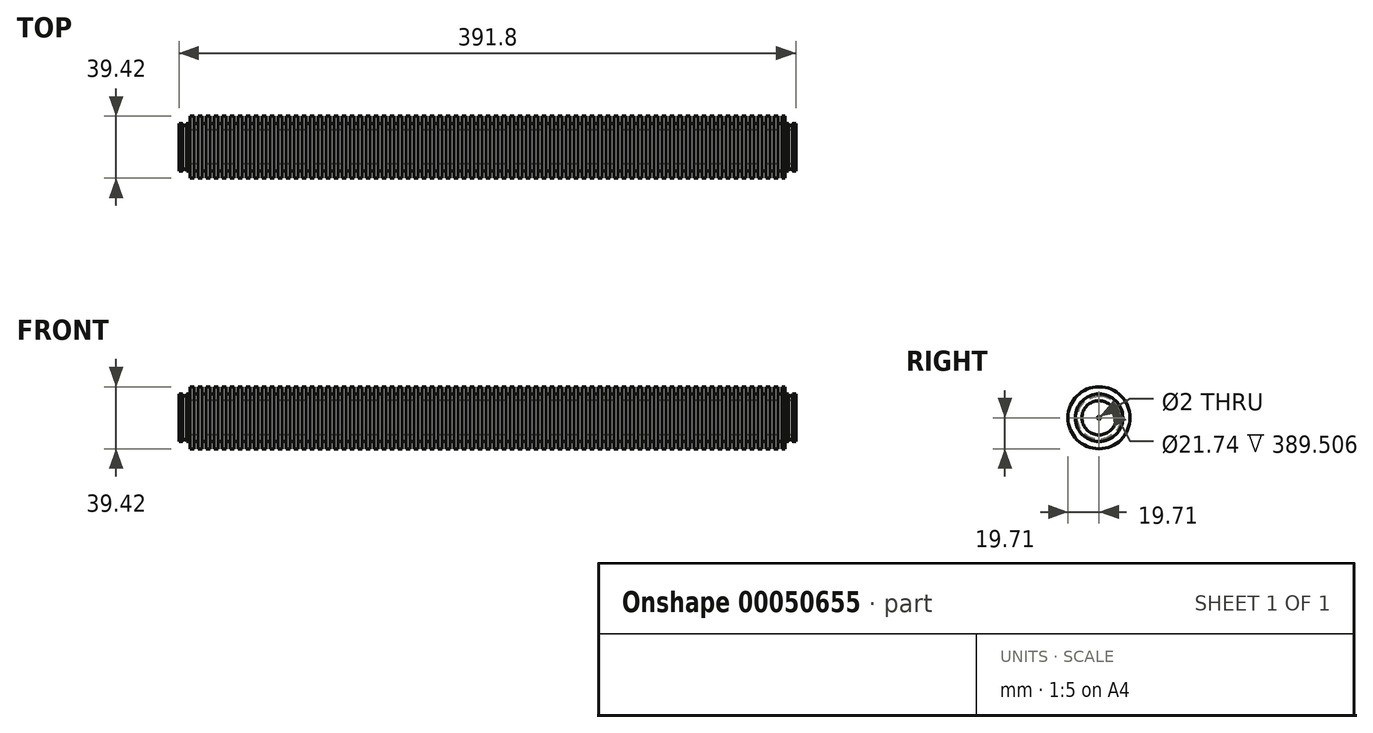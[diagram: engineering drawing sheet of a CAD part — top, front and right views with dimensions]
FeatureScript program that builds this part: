
annotation { "Feature Type Name" : "Feature", "Feature Type Description" : "" }
export const myFeature = defineFeature(function(context is Context, id is Id, definition is map)
    precondition{}
    {
        {
            var Q0;
            Q0=qCreatedBy(makeId("Front.planeOp"),FACE);
            var sketch = newSketch(context, id + "F0", { "sketchPlane" : qUnion([Q0])});
            skLineSegment(sketch, "E0", {"start": v(0, 15.1) * mm, "end": v(2.23, 15.1) * mm});
            skLineSegment(sketch, "E1", {"start": v(7, 15.1) * mm, "end": v(7, 19.7) * mm});
            skLineSegment(sketch, "E2", {"start": v(7, 19.7) * mm, "end": v(9.54, 19.7) * mm});
            skLineSegment(sketch, "E3", {"start": v(384.8, 19.71) * mm, "end": v(384.8, 15.1) * mm});
            skLineSegment(sketch, "E4", {"start": v(391.8, 15.1) * mm, "end": v(391.8, 10.87) * mm});
            skLineSegment(sketch, "E5", {"start": v(391.8, 10.87) * mm, "end": v(2.29, 10.87) * mm});
            skLineSegment(sketch, "E6", {"start": v(0, 15.1) * mm, "end": v(0, 10.87) * mm});
            skArc(sketch, "E7", {"start": v(2.23, 15.1) * mm, "mid": v(3.5, 13.83) * mm, "end": v(4.77, 15.1) * mm});
            skLineSegment(sketch, "E8.trimOffspring", {"start": v(4.77, 15.1) * mm, "end": v(7, 15.1) * mm});
            skLineSegment(sketch, "E9", {"start": v(384.8, 15.1) * mm, "end": v(387.03, 15.1) * mm});
            skArc(sketch, "E10", {"start": v(387.03, 15.1) * mm, "mid": v(388.3, 13.83) * mm, "end": v(389.57, 15.1) * mm});
            skLineSegment(sketch, "E11.trimOffspring", {"start": v(389.57, 15.1) * mm, "end": v(391.8, 15.1) * mm});
            skLineSegment(sketch, "E12", {"start": v(0, 10.87) * mm, "end": v(0, 1) * mm});
            skLineSegment(sketch, "E13", {"start": v(0, 1) * mm, "end": v(2.29, 1) * mm});
            skLineSegment(sketch, "E14", {"start": v(2.29, 1) * mm, "end": v(2.29, 10.87) * mm});
            skLineSegment(sketch, "E15", {"start": v(9.54, 19.7) * mm, "end": v(9.54, 15.1) * mm});
            skLineSegment(sketch, "E16", {"start": v(9.54, 15.1) * mm, "end": v(12.08, 15.1) * mm});
            skLineSegment(sketch, "E17", {"start": v(12.08, 15.1) * mm, "end": v(12.08, 19.71) * mm});
            skLineSegment(sketch, "E18.1.0.0", {"start": v(12.08, 19.7) * mm, "end": v(14.62, 19.7) * mm});
            skLineSegment(sketch, "E18.1.0.1", {"start": v(17.16, 15.1) * mm, "end": v(17.16, 19.71) * mm});
            skLineSegment(sketch, "E18.1.0.2", {"start": v(14.62, 19.7) * mm, "end": v(14.62, 15.1) * mm});
            skLineSegment(sketch, "E18.1.0.3", {"start": v(14.62, 15.1) * mm, "end": v(17.16, 15.1) * mm});
            skLineSegment(sketch, "E18.2.0.0", {"start": v(17.16, 19.7) * mm, "end": v(19.7, 19.7) * mm});
            skLineSegment(sketch, "E18.2.0.1", {"start": v(22.24, 15.1) * mm, "end": v(22.24, 19.71) * mm});
            skLineSegment(sketch, "E18.2.0.2", {"start": v(19.7, 19.7) * mm, "end": v(19.7, 15.1) * mm});
            skLineSegment(sketch, "E18.2.0.3", {"start": v(19.7, 15.1) * mm, "end": v(22.24, 15.1) * mm});
            skLineSegment(sketch, "E18.3.0.0", {"start": v(22.24, 19.7) * mm, "end": v(24.78, 19.7) * mm});
            skLineSegment(sketch, "E18.3.0.1", {"start": v(27.32, 15.1) * mm, "end": v(27.32, 19.71) * mm});
            skLineSegment(sketch, "E18.3.0.2", {"start": v(24.78, 19.7) * mm, "end": v(24.78, 15.1) * mm});
            skLineSegment(sketch, "E18.3.0.3", {"start": v(24.78, 15.1) * mm, "end": v(27.32, 15.1) * mm});
            skLineSegment(sketch, "E18.4.0.0", {"start": v(27.32, 19.7) * mm, "end": v(29.86, 19.7) * mm});
            skLineSegment(sketch, "E18.4.0.1", {"start": v(32.4, 15.1) * mm, "end": v(32.4, 19.71) * mm});
            skLineSegment(sketch, "E18.4.0.2", {"start": v(29.86, 19.7) * mm, "end": v(29.86, 15.1) * mm});
            skLineSegment(sketch, "E18.4.0.3", {"start": v(29.86, 15.1) * mm, "end": v(32.4, 15.1) * mm});
            skLineSegment(sketch, "E18.5.0.0", {"start": v(32.4, 19.7) * mm, "end": v(34.94, 19.7) * mm});
            skLineSegment(sketch, "E18.5.0.1", {"start": v(37.48, 15.1) * mm, "end": v(37.48, 19.71) * mm});
            skLineSegment(sketch, "E18.5.0.2", {"start": v(34.94, 19.7) * mm, "end": v(34.94, 15.1) * mm});
            skLineSegment(sketch, "E18.5.0.3", {"start": v(34.94, 15.1) * mm, "end": v(37.48, 15.1) * mm});
            skLineSegment(sketch, "E18.6.0.0", {"start": v(37.48, 19.7) * mm, "end": v(40.02, 19.7) * mm});
            skLineSegment(sketch, "E18.6.0.1", {"start": v(42.56, 15.1) * mm, "end": v(42.56, 19.71) * mm});
            skLineSegment(sketch, "E18.6.0.2", {"start": v(40.02, 19.7) * mm, "end": v(40.02, 15.1) * mm});
            skLineSegment(sketch, "E18.6.0.3", {"start": v(40.02, 15.1) * mm, "end": v(42.56, 15.1) * mm});
            skLineSegment(sketch, "E18.7.0.0", {"start": v(42.56, 19.7) * mm, "end": v(45.1, 19.7) * mm});
            skLineSegment(sketch, "E18.7.0.1", {"start": v(47.64, 15.1) * mm, "end": v(47.64, 19.71) * mm});
            skLineSegment(sketch, "E18.7.0.2", {"start": v(45.1, 19.7) * mm, "end": v(45.1, 15.1) * mm});
            skLineSegment(sketch, "E18.7.0.3", {"start": v(45.1, 15.1) * mm, "end": v(47.64, 15.1) * mm});
            skLineSegment(sketch, "E18.8.0.0", {"start": v(47.64, 19.7) * mm, "end": v(50.18, 19.7) * mm});
            skLineSegment(sketch, "E18.8.0.1", {"start": v(52.72, 15.1) * mm, "end": v(52.72, 19.71) * mm});
            skLineSegment(sketch, "E18.8.0.2", {"start": v(50.18, 19.7) * mm, "end": v(50.18, 15.1) * mm});
            skLineSegment(sketch, "E18.8.0.3", {"start": v(50.18, 15.1) * mm, "end": v(52.72, 15.1) * mm});
            skLineSegment(sketch, "E18.9.0.0", {"start": v(52.72, 19.7) * mm, "end": v(55.26, 19.7) * mm});
            skLineSegment(sketch, "E18.9.0.1", {"start": v(57.8, 15.1) * mm, "end": v(57.8, 19.71) * mm});
            skLineSegment(sketch, "E18.9.0.2", {"start": v(55.26, 19.7) * mm, "end": v(55.26, 15.1) * mm});
            skLineSegment(sketch, "E18.9.0.3", {"start": v(55.26, 15.1) * mm, "end": v(57.8, 15.1) * mm});
            skLineSegment(sketch, "E18.10.0.0", {"start": v(57.8, 19.7) * mm, "end": v(60.34, 19.7) * mm});
            skLineSegment(sketch, "E18.10.0.1", {"start": v(62.88, 15.1) * mm, "end": v(62.88, 19.71) * mm});
            skLineSegment(sketch, "E18.10.0.2", {"start": v(60.34, 19.7) * mm, "end": v(60.34, 15.1) * mm});
            skLineSegment(sketch, "E18.10.0.3", {"start": v(60.34, 15.1) * mm, "end": v(62.88, 15.1) * mm});
            skLineSegment(sketch, "E18.11.0.0", {"start": v(62.88, 19.7) * mm, "end": v(65.42, 19.7) * mm});
            skLineSegment(sketch, "E18.11.0.1", {"start": v(67.96, 15.1) * mm, "end": v(67.96, 19.71) * mm});
            skLineSegment(sketch, "E18.11.0.2", {"start": v(65.42, 19.7) * mm, "end": v(65.42, 15.1) * mm});
            skLineSegment(sketch, "E18.11.0.3", {"start": v(65.42, 15.1) * mm, "end": v(67.96, 15.1) * mm});
            skLineSegment(sketch, "E18.12.0.0", {"start": v(67.96, 19.7) * mm, "end": v(70.5, 19.7) * mm});
            skLineSegment(sketch, "E18.12.0.1", {"start": v(73.04, 15.1) * mm, "end": v(73.04, 19.71) * mm});
            skLineSegment(sketch, "E18.12.0.2", {"start": v(70.5, 19.7) * mm, "end": v(70.5, 15.1) * mm});
            skLineSegment(sketch, "E18.12.0.3", {"start": v(70.5, 15.1) * mm, "end": v(73.04, 15.1) * mm});
            skLineSegment(sketch, "E18.13.0.0", {"start": v(73.04, 19.7) * mm, "end": v(75.58, 19.7) * mm});
            skLineSegment(sketch, "E18.13.0.1", {"start": v(78.12, 15.1) * mm, "end": v(78.12, 19.71) * mm});
            skLineSegment(sketch, "E18.13.0.2", {"start": v(75.58, 19.7) * mm, "end": v(75.58, 15.1) * mm});
            skLineSegment(sketch, "E18.13.0.3", {"start": v(75.58, 15.1) * mm, "end": v(78.12, 15.1) * mm});
            skLineSegment(sketch, "E18.14.0.0", {"start": v(78.12, 19.7) * mm, "end": v(80.66, 19.7) * mm});
            skLineSegment(sketch, "E18.14.0.1", {"start": v(83.2, 15.1) * mm, "end": v(83.2, 19.71) * mm});
            skLineSegment(sketch, "E18.14.0.2", {"start": v(80.66, 19.7) * mm, "end": v(80.66, 15.1) * mm});
            skLineSegment(sketch, "E18.14.0.3", {"start": v(80.66, 15.1) * mm, "end": v(83.2, 15.1) * mm});
            skLineSegment(sketch, "E18.15.0.0", {"start": v(83.2, 19.7) * mm, "end": v(85.74, 19.7) * mm});
            skLineSegment(sketch, "E18.15.0.1", {"start": v(88.28, 15.1) * mm, "end": v(88.28, 19.71) * mm});
            skLineSegment(sketch, "E18.15.0.2", {"start": v(85.74, 19.7) * mm, "end": v(85.74, 15.1) * mm});
            skLineSegment(sketch, "E18.15.0.3", {"start": v(85.74, 15.1) * mm, "end": v(88.28, 15.1) * mm});
            skLineSegment(sketch, "E18.16.0.0", {"start": v(88.28, 19.7) * mm, "end": v(90.82, 19.7) * mm});
            skLineSegment(sketch, "E18.16.0.1", {"start": v(93.36, 15.1) * mm, "end": v(93.36, 19.71) * mm});
            skLineSegment(sketch, "E18.16.0.2", {"start": v(90.82, 19.7) * mm, "end": v(90.82, 15.1) * mm});
            skLineSegment(sketch, "E18.16.0.3", {"start": v(90.82, 15.1) * mm, "end": v(93.36, 15.1) * mm});
            skLineSegment(sketch, "E18.17.0.0", {"start": v(93.36, 19.7) * mm, "end": v(95.9, 19.7) * mm});
            skLineSegment(sketch, "E18.17.0.1", {"start": v(98.44, 15.1) * mm, "end": v(98.44, 19.71) * mm});
            skLineSegment(sketch, "E18.17.0.2", {"start": v(95.9, 19.7) * mm, "end": v(95.9, 15.1) * mm});
            skLineSegment(sketch, "E18.17.0.3", {"start": v(95.9, 15.1) * mm, "end": v(98.44, 15.1) * mm});
            skLineSegment(sketch, "E18.18.0.0", {"start": v(98.44, 19.7) * mm, "end": v(100.98, 19.7) * mm});
            skLineSegment(sketch, "E18.18.0.1", {"start": v(103.52, 15.1) * mm, "end": v(103.52, 19.71) * mm});
            skLineSegment(sketch, "E18.18.0.2", {"start": v(100.98, 19.7) * mm, "end": v(100.98, 15.1) * mm});
            skLineSegment(sketch, "E18.18.0.3", {"start": v(100.98, 15.1) * mm, "end": v(103.52, 15.1) * mm});
            skLineSegment(sketch, "E18.19.0.0", {"start": v(103.52, 19.7) * mm, "end": v(106.06, 19.7) * mm});
            skLineSegment(sketch, "E18.19.0.1", {"start": v(108.6, 15.1) * mm, "end": v(108.6, 19.71) * mm});
            skLineSegment(sketch, "E18.19.0.2", {"start": v(106.06, 19.7) * mm, "end": v(106.06, 15.1) * mm});
            skLineSegment(sketch, "E18.19.0.3", {"start": v(106.06, 15.1) * mm, "end": v(108.6, 15.1) * mm});
            skLineSegment(sketch, "E18.20.0.0", {"start": v(108.6, 19.7) * mm, "end": v(111.14, 19.7) * mm});
            skLineSegment(sketch, "E18.20.0.1", {"start": v(113.68, 15.1) * mm, "end": v(113.68, 19.71) * mm});
            skLineSegment(sketch, "E18.20.0.2", {"start": v(111.14, 19.7) * mm, "end": v(111.14, 15.1) * mm});
            skLineSegment(sketch, "E18.20.0.3", {"start": v(111.14, 15.1) * mm, "end": v(113.68, 15.1) * mm});
            skLineSegment(sketch, "E18.21.0.0", {"start": v(113.68, 19.7) * mm, "end": v(116.22, 19.7) * mm});
            skLineSegment(sketch, "E18.21.0.1", {"start": v(118.76, 15.1) * mm, "end": v(118.76, 19.71) * mm});
            skLineSegment(sketch, "E18.21.0.2", {"start": v(116.22, 19.7) * mm, "end": v(116.22, 15.1) * mm});
            skLineSegment(sketch, "E18.21.0.3", {"start": v(116.22, 15.1) * mm, "end": v(118.76, 15.1) * mm});
            skLineSegment(sketch, "E18.22.0.0", {"start": v(118.76, 19.7) * mm, "end": v(121.3, 19.7) * mm});
            skLineSegment(sketch, "E18.22.0.1", {"start": v(123.84, 15.1) * mm, "end": v(123.84, 19.71) * mm});
            skLineSegment(sketch, "E18.22.0.2", {"start": v(121.3, 19.7) * mm, "end": v(121.3, 15.1) * mm});
            skLineSegment(sketch, "E18.22.0.3", {"start": v(121.3, 15.1) * mm, "end": v(123.84, 15.1) * mm});
            skLineSegment(sketch, "E18.23.0.0", {"start": v(123.84, 19.7) * mm, "end": v(126.38, 19.7) * mm});
            skLineSegment(sketch, "E18.23.0.1", {"start": v(128.92, 15.1) * mm, "end": v(128.92, 19.71) * mm});
            skLineSegment(sketch, "E18.23.0.2", {"start": v(126.38, 19.7) * mm, "end": v(126.38, 15.1) * mm});
            skLineSegment(sketch, "E18.23.0.3", {"start": v(126.38, 15.1) * mm, "end": v(128.92, 15.1) * mm});
            skLineSegment(sketch, "E18.24.0.0", {"start": v(128.92, 19.7) * mm, "end": v(131.46, 19.7) * mm});
            skLineSegment(sketch, "E18.24.0.1", {"start": v(134, 15.1) * mm, "end": v(134, 19.71) * mm});
            skLineSegment(sketch, "E18.24.0.2", {"start": v(131.46, 19.7) * mm, "end": v(131.46, 15.1) * mm});
            skLineSegment(sketch, "E18.24.0.3", {"start": v(131.46, 15.1) * mm, "end": v(134, 15.1) * mm});
            skLineSegment(sketch, "E18.25.0.0", {"start": v(134, 19.7) * mm, "end": v(136.54, 19.7) * mm});
            skLineSegment(sketch, "E18.25.0.1", {"start": v(139.08, 15.1) * mm, "end": v(139.08, 19.71) * mm});
            skLineSegment(sketch, "E18.25.0.2", {"start": v(136.54, 19.7) * mm, "end": v(136.54, 15.1) * mm});
            skLineSegment(sketch, "E18.25.0.3", {"start": v(136.54, 15.1) * mm, "end": v(139.08, 15.1) * mm});
            skLineSegment(sketch, "E18.26.0.0", {"start": v(139.08, 19.7) * mm, "end": v(141.62, 19.7) * mm});
            skLineSegment(sketch, "E18.26.0.1", {"start": v(144.16, 15.1) * mm, "end": v(144.16, 19.71) * mm});
            skLineSegment(sketch, "E18.26.0.2", {"start": v(141.62, 19.7) * mm, "end": v(141.62, 15.1) * mm});
            skLineSegment(sketch, "E18.26.0.3", {"start": v(141.62, 15.1) * mm, "end": v(144.16, 15.1) * mm});
            skLineSegment(sketch, "E18.27.0.0", {"start": v(144.16, 19.7) * mm, "end": v(146.7, 19.7) * mm});
            skLineSegment(sketch, "E18.27.0.1", {"start": v(149.24, 15.1) * mm, "end": v(149.24, 19.71) * mm});
            skLineSegment(sketch, "E18.27.0.2", {"start": v(146.7, 19.7) * mm, "end": v(146.7, 15.1) * mm});
            skLineSegment(sketch, "E18.27.0.3", {"start": v(146.7, 15.1) * mm, "end": v(149.24, 15.1) * mm});
            skLineSegment(sketch, "E18.28.0.0", {"start": v(149.24, 19.7) * mm, "end": v(151.78, 19.7) * mm});
            skLineSegment(sketch, "E18.28.0.1", {"start": v(154.32, 15.1) * mm, "end": v(154.32, 19.71) * mm});
            skLineSegment(sketch, "E18.28.0.2", {"start": v(151.78, 19.7) * mm, "end": v(151.78, 15.1) * mm});
            skLineSegment(sketch, "E18.28.0.3", {"start": v(151.78, 15.1) * mm, "end": v(154.32, 15.1) * mm});
            skLineSegment(sketch, "E18.29.0.0", {"start": v(154.32, 19.7) * mm, "end": v(156.86, 19.7) * mm});
            skLineSegment(sketch, "E18.29.0.1", {"start": v(159.4, 15.1) * mm, "end": v(159.4, 19.71) * mm});
            skLineSegment(sketch, "E18.29.0.2", {"start": v(156.86, 19.7) * mm, "end": v(156.86, 15.1) * mm});
            skLineSegment(sketch, "E18.29.0.3", {"start": v(156.86, 15.1) * mm, "end": v(159.4, 15.1) * mm});
            skLineSegment(sketch, "E18.30.0.0", {"start": v(159.4, 19.7) * mm, "end": v(161.94, 19.7) * mm});
            skLineSegment(sketch, "E18.30.0.1", {"start": v(164.48, 15.1) * mm, "end": v(164.48, 19.71) * mm});
            skLineSegment(sketch, "E18.30.0.2", {"start": v(161.94, 19.7) * mm, "end": v(161.94, 15.1) * mm});
            skLineSegment(sketch, "E18.30.0.3", {"start": v(161.94, 15.1) * mm, "end": v(164.48, 15.1) * mm});
            skLineSegment(sketch, "E18.31.0.0", {"start": v(164.48, 19.7) * mm, "end": v(167.02, 19.7) * mm});
            skLineSegment(sketch, "E18.31.0.1", {"start": v(169.56, 15.1) * mm, "end": v(169.56, 19.71) * mm});
            skLineSegment(sketch, "E18.31.0.2", {"start": v(167.02, 19.7) * mm, "end": v(167.02, 15.1) * mm});
            skLineSegment(sketch, "E18.31.0.3", {"start": v(167.02, 15.1) * mm, "end": v(169.56, 15.1) * mm});
            skLineSegment(sketch, "E18.32.0.0", {"start": v(169.56, 19.7) * mm, "end": v(172.1, 19.7) * mm});
            skLineSegment(sketch, "E18.32.0.1", {"start": v(174.64, 15.1) * mm, "end": v(174.64, 19.71) * mm});
            skLineSegment(sketch, "E18.32.0.2", {"start": v(172.1, 19.7) * mm, "end": v(172.1, 15.1) * mm});
            skLineSegment(sketch, "E18.32.0.3", {"start": v(172.1, 15.1) * mm, "end": v(174.64, 15.1) * mm});
            skLineSegment(sketch, "E18.33.0.0", {"start": v(174.64, 19.7) * mm, "end": v(177.18, 19.7) * mm});
            skLineSegment(sketch, "E18.33.0.1", {"start": v(179.72, 15.1) * mm, "end": v(179.72, 19.71) * mm});
            skLineSegment(sketch, "E18.33.0.2", {"start": v(177.18, 19.7) * mm, "end": v(177.18, 15.1) * mm});
            skLineSegment(sketch, "E18.33.0.3", {"start": v(177.18, 15.1) * mm, "end": v(179.72, 15.1) * mm});
            skLineSegment(sketch, "E18.34.0.0", {"start": v(179.72, 19.7) * mm, "end": v(182.26, 19.7) * mm});
            skLineSegment(sketch, "E18.34.0.1", {"start": v(184.8, 15.1) * mm, "end": v(184.8, 19.71) * mm});
            skLineSegment(sketch, "E18.34.0.2", {"start": v(182.26, 19.7) * mm, "end": v(182.26, 15.1) * mm});
            skLineSegment(sketch, "E18.34.0.3", {"start": v(182.26, 15.1) * mm, "end": v(184.8, 15.1) * mm});
            skLineSegment(sketch, "E18.35.0.0", {"start": v(184.8, 19.7) * mm, "end": v(187.34, 19.7) * mm});
            skLineSegment(sketch, "E18.35.0.1", {"start": v(189.88, 15.1) * mm, "end": v(189.88, 19.71) * mm});
            skLineSegment(sketch, "E18.35.0.2", {"start": v(187.34, 19.7) * mm, "end": v(187.34, 15.1) * mm});
            skLineSegment(sketch, "E18.35.0.3", {"start": v(187.34, 15.1) * mm, "end": v(189.88, 15.1) * mm});
            skLineSegment(sketch, "E18.36.0.0", {"start": v(189.88, 19.7) * mm, "end": v(192.42, 19.7) * mm});
            skLineSegment(sketch, "E18.36.0.1", {"start": v(194.96, 15.1) * mm, "end": v(194.96, 19.71) * mm});
            skLineSegment(sketch, "E18.36.0.2", {"start": v(192.42, 19.7) * mm, "end": v(192.42, 15.1) * mm});
            skLineSegment(sketch, "E18.36.0.3", {"start": v(192.42, 15.1) * mm, "end": v(194.96, 15.1) * mm});
            skLineSegment(sketch, "E18.37.0.0", {"start": v(194.96, 19.7) * mm, "end": v(197.5, 19.7) * mm});
            skLineSegment(sketch, "E18.37.0.1", {"start": v(200.04, 15.1) * mm, "end": v(200.04, 19.71) * mm});
            skLineSegment(sketch, "E18.37.0.2", {"start": v(197.5, 19.7) * mm, "end": v(197.5, 15.1) * mm});
            skLineSegment(sketch, "E18.37.0.3", {"start": v(197.5, 15.1) * mm, "end": v(200.04, 15.1) * mm});
            skLineSegment(sketch, "E18.38.0.0", {"start": v(200.04, 19.7) * mm, "end": v(202.58, 19.7) * mm});
            skLineSegment(sketch, "E18.38.0.1", {"start": v(205.12, 15.1) * mm, "end": v(205.12, 19.71) * mm});
            skLineSegment(sketch, "E18.38.0.2", {"start": v(202.58, 19.7) * mm, "end": v(202.58, 15.1) * mm});
            skLineSegment(sketch, "E18.38.0.3", {"start": v(202.58, 15.1) * mm, "end": v(205.12, 15.1) * mm});
            skLineSegment(sketch, "E18.39.0.0", {"start": v(205.12, 19.7) * mm, "end": v(207.66, 19.7) * mm});
            skLineSegment(sketch, "E18.39.0.1", {"start": v(210.2, 15.1) * mm, "end": v(210.2, 19.71) * mm});
            skLineSegment(sketch, "E18.39.0.2", {"start": v(207.66, 19.7) * mm, "end": v(207.66, 15.1) * mm});
            skLineSegment(sketch, "E18.39.0.3", {"start": v(207.66, 15.1) * mm, "end": v(210.2, 15.1) * mm});
            skLineSegment(sketch, "E18.40.0.0", {"start": v(210.2, 19.7) * mm, "end": v(212.74, 19.7) * mm});
            skLineSegment(sketch, "E18.40.0.1", {"start": v(215.28, 15.1) * mm, "end": v(215.28, 19.71) * mm});
            skLineSegment(sketch, "E18.40.0.2", {"start": v(212.74, 19.7) * mm, "end": v(212.74, 15.1) * mm});
            skLineSegment(sketch, "E18.40.0.3", {"start": v(212.74, 15.1) * mm, "end": v(215.28, 15.1) * mm});
            skLineSegment(sketch, "E18.41.0.0", {"start": v(215.28, 19.7) * mm, "end": v(217.82, 19.7) * mm});
            skLineSegment(sketch, "E18.41.0.1", {"start": v(220.36, 15.1) * mm, "end": v(220.36, 19.71) * mm});
            skLineSegment(sketch, "E18.41.0.2", {"start": v(217.82, 19.7) * mm, "end": v(217.82, 15.1) * mm});
            skLineSegment(sketch, "E18.41.0.3", {"start": v(217.82, 15.1) * mm, "end": v(220.36, 15.1) * mm});
            skLineSegment(sketch, "E18.42.0.0", {"start": v(220.36, 19.7) * mm, "end": v(222.9, 19.7) * mm});
            skLineSegment(sketch, "E18.42.0.1", {"start": v(225.44, 15.1) * mm, "end": v(225.44, 19.71) * mm});
            skLineSegment(sketch, "E18.42.0.2", {"start": v(222.9, 19.7) * mm, "end": v(222.9, 15.1) * mm});
            skLineSegment(sketch, "E18.42.0.3", {"start": v(222.9, 15.1) * mm, "end": v(225.44, 15.1) * mm});
            skLineSegment(sketch, "E18.43.0.0", {"start": v(225.44, 19.7) * mm, "end": v(227.98, 19.7) * mm});
            skLineSegment(sketch, "E18.43.0.1", {"start": v(230.52, 15.1) * mm, "end": v(230.52, 19.71) * mm});
            skLineSegment(sketch, "E18.43.0.2", {"start": v(227.98, 19.7) * mm, "end": v(227.98, 15.1) * mm});
            skLineSegment(sketch, "E18.43.0.3", {"start": v(227.98, 15.1) * mm, "end": v(230.52, 15.1) * mm});
            skLineSegment(sketch, "E18.44.0.0", {"start": v(230.52, 19.7) * mm, "end": v(233.06, 19.7) * mm});
            skLineSegment(sketch, "E18.44.0.1", {"start": v(235.6, 15.1) * mm, "end": v(235.6, 19.71) * mm});
            skLineSegment(sketch, "E18.44.0.2", {"start": v(233.06, 19.7) * mm, "end": v(233.06, 15.1) * mm});
            skLineSegment(sketch, "E18.44.0.3", {"start": v(233.06, 15.1) * mm, "end": v(235.6, 15.1) * mm});
            skLineSegment(sketch, "E18.45.0.0", {"start": v(235.6, 19.7) * mm, "end": v(238.14, 19.7) * mm});
            skLineSegment(sketch, "E18.45.0.1", {"start": v(240.68, 15.1) * mm, "end": v(240.68, 19.71) * mm});
            skLineSegment(sketch, "E18.45.0.2", {"start": v(238.14, 19.7) * mm, "end": v(238.14, 15.1) * mm});
            skLineSegment(sketch, "E18.45.0.3", {"start": v(238.14, 15.1) * mm, "end": v(240.68, 15.1) * mm});
            skLineSegment(sketch, "E18.46.0.0", {"start": v(240.68, 19.7) * mm, "end": v(243.22, 19.7) * mm});
            skLineSegment(sketch, "E18.46.0.1", {"start": v(245.76, 15.1) * mm, "end": v(245.76, 19.71) * mm});
            skLineSegment(sketch, "E18.46.0.2", {"start": v(243.22, 19.7) * mm, "end": v(243.22, 15.1) * mm});
            skLineSegment(sketch, "E18.46.0.3", {"start": v(243.22, 15.1) * mm, "end": v(245.76, 15.1) * mm});
            skLineSegment(sketch, "E18.47.0.0", {"start": v(245.76, 19.7) * mm, "end": v(248.3, 19.7) * mm});
            skLineSegment(sketch, "E18.47.0.1", {"start": v(250.84, 15.1) * mm, "end": v(250.84, 19.71) * mm});
            skLineSegment(sketch, "E18.47.0.2", {"start": v(248.3, 19.7) * mm, "end": v(248.3, 15.1) * mm});
            skLineSegment(sketch, "E18.47.0.3", {"start": v(248.3, 15.1) * mm, "end": v(250.84, 15.1) * mm});
            skLineSegment(sketch, "E18.48.0.0", {"start": v(250.84, 19.7) * mm, "end": v(253.38, 19.7) * mm});
            skLineSegment(sketch, "E18.48.0.1", {"start": v(255.92, 15.1) * mm, "end": v(255.92, 19.71) * mm});
            skLineSegment(sketch, "E18.48.0.2", {"start": v(253.38, 19.7) * mm, "end": v(253.38, 15.1) * mm});
            skLineSegment(sketch, "E18.48.0.3", {"start": v(253.38, 15.1) * mm, "end": v(255.92, 15.1) * mm});
            skLineSegment(sketch, "E18.49.0.0", {"start": v(255.92, 19.7) * mm, "end": v(258.46, 19.7) * mm});
            skLineSegment(sketch, "E18.49.0.1", {"start": v(261, 15.1) * mm, "end": v(261, 19.71) * mm});
            skLineSegment(sketch, "E18.49.0.2", {"start": v(258.46, 19.7) * mm, "end": v(258.46, 15.1) * mm});
            skLineSegment(sketch, "E18.49.0.3", {"start": v(258.46, 15.1) * mm, "end": v(261, 15.1) * mm});
            skLineSegment(sketch, "E18.50.0.0", {"start": v(261, 19.7) * mm, "end": v(263.54, 19.7) * mm});
            skLineSegment(sketch, "E18.50.0.1", {"start": v(266.08, 15.1) * mm, "end": v(266.08, 19.71) * mm});
            skLineSegment(sketch, "E18.50.0.2", {"start": v(263.54, 19.7) * mm, "end": v(263.54, 15.1) * mm});
            skLineSegment(sketch, "E18.50.0.3", {"start": v(263.54, 15.1) * mm, "end": v(266.08, 15.1) * mm});
            skLineSegment(sketch, "E18.51.0.0", {"start": v(266.08, 19.7) * mm, "end": v(268.62, 19.7) * mm});
            skLineSegment(sketch, "E18.51.0.1", {"start": v(271.16, 15.1) * mm, "end": v(271.16, 19.71) * mm});
            skLineSegment(sketch, "E18.51.0.2", {"start": v(268.62, 19.7) * mm, "end": v(268.62, 15.1) * mm});
            skLineSegment(sketch, "E18.51.0.3", {"start": v(268.62, 15.1) * mm, "end": v(271.16, 15.1) * mm});
            skLineSegment(sketch, "E18.52.0.0", {"start": v(271.16, 19.7) * mm, "end": v(273.7, 19.7) * mm});
            skLineSegment(sketch, "E18.52.0.1", {"start": v(276.24, 15.1) * mm, "end": v(276.24, 19.71) * mm});
            skLineSegment(sketch, "E18.52.0.2", {"start": v(273.7, 19.7) * mm, "end": v(273.7, 15.1) * mm});
            skLineSegment(sketch, "E18.52.0.3", {"start": v(273.7, 15.1) * mm, "end": v(276.24, 15.1) * mm});
            skLineSegment(sketch, "E18.53.0.0", {"start": v(276.24, 19.7) * mm, "end": v(278.78, 19.7) * mm});
            skLineSegment(sketch, "E18.53.0.1", {"start": v(281.32, 15.1) * mm, "end": v(281.32, 19.71) * mm});
            skLineSegment(sketch, "E18.53.0.2", {"start": v(278.78, 19.7) * mm, "end": v(278.78, 15.1) * mm});
            skLineSegment(sketch, "E18.53.0.3", {"start": v(278.78, 15.1) * mm, "end": v(281.32, 15.1) * mm});
            skLineSegment(sketch, "E18.54.0.0", {"start": v(281.32, 19.7) * mm, "end": v(283.86, 19.7) * mm});
            skLineSegment(sketch, "E18.54.0.1", {"start": v(286.4, 15.1) * mm, "end": v(286.4, 19.71) * mm});
            skLineSegment(sketch, "E18.54.0.2", {"start": v(283.86, 19.7) * mm, "end": v(283.86, 15.1) * mm});
            skLineSegment(sketch, "E18.54.0.3", {"start": v(283.86, 15.1) * mm, "end": v(286.4, 15.1) * mm});
            skLineSegment(sketch, "E18.55.0.0", {"start": v(286.4, 19.7) * mm, "end": v(288.94, 19.7) * mm});
            skLineSegment(sketch, "E18.55.0.1", {"start": v(291.48, 15.1) * mm, "end": v(291.48, 19.71) * mm});
            skLineSegment(sketch, "E18.55.0.2", {"start": v(288.94, 19.7) * mm, "end": v(288.94, 15.1) * mm});
            skLineSegment(sketch, "E18.55.0.3", {"start": v(288.94, 15.1) * mm, "end": v(291.48, 15.1) * mm});
            skLineSegment(sketch, "E18.56.0.0", {"start": v(291.48, 19.7) * mm, "end": v(294.02, 19.7) * mm});
            skLineSegment(sketch, "E18.56.0.1", {"start": v(296.56, 15.1) * mm, "end": v(296.56, 19.71) * mm});
            skLineSegment(sketch, "E18.56.0.2", {"start": v(294.02, 19.7) * mm, "end": v(294.02, 15.1) * mm});
            skLineSegment(sketch, "E18.56.0.3", {"start": v(294.02, 15.1) * mm, "end": v(296.56, 15.1) * mm});
            skLineSegment(sketch, "E18.57.0.0", {"start": v(296.56, 19.7) * mm, "end": v(299.1, 19.7) * mm});
            skLineSegment(sketch, "E18.57.0.1", {"start": v(301.64, 15.1) * mm, "end": v(301.64, 19.71) * mm});
            skLineSegment(sketch, "E18.57.0.2", {"start": v(299.1, 19.7) * mm, "end": v(299.1, 15.1) * mm});
            skLineSegment(sketch, "E18.57.0.3", {"start": v(299.1, 15.1) * mm, "end": v(301.64, 15.1) * mm});
            skLineSegment(sketch, "E18.58.0.0", {"start": v(301.64, 19.7) * mm, "end": v(304.18, 19.7) * mm});
            skLineSegment(sketch, "E18.58.0.1", {"start": v(306.72, 15.1) * mm, "end": v(306.72, 19.71) * mm});
            skLineSegment(sketch, "E18.58.0.2", {"start": v(304.18, 19.7) * mm, "end": v(304.18, 15.1) * mm});
            skLineSegment(sketch, "E18.58.0.3", {"start": v(304.18, 15.1) * mm, "end": v(306.72, 15.1) * mm});
            skLineSegment(sketch, "E18.59.0.0", {"start": v(306.72, 19.7) * mm, "end": v(309.26, 19.7) * mm});
            skLineSegment(sketch, "E18.59.0.1", {"start": v(311.8, 15.1) * mm, "end": v(311.8, 19.71) * mm});
            skLineSegment(sketch, "E18.59.0.2", {"start": v(309.26, 19.7) * mm, "end": v(309.26, 15.1) * mm});
            skLineSegment(sketch, "E18.59.0.3", {"start": v(309.26, 15.1) * mm, "end": v(311.8, 15.1) * mm});
            skLineSegment(sketch, "E18.60.0.0", {"start": v(311.8, 19.7) * mm, "end": v(314.34, 19.7) * mm});
            skLineSegment(sketch, "E18.60.0.1", {"start": v(316.88, 15.1) * mm, "end": v(316.88, 19.71) * mm});
            skLineSegment(sketch, "E18.60.0.2", {"start": v(314.34, 19.7) * mm, "end": v(314.34, 15.1) * mm});
            skLineSegment(sketch, "E18.60.0.3", {"start": v(314.34, 15.1) * mm, "end": v(316.88, 15.1) * mm});
            skLineSegment(sketch, "E18.61.0.0", {"start": v(316.88, 19.7) * mm, "end": v(319.42, 19.7) * mm});
            skLineSegment(sketch, "E18.61.0.1", {"start": v(321.96, 15.1) * mm, "end": v(321.96, 19.71) * mm});
            skLineSegment(sketch, "E18.61.0.2", {"start": v(319.42, 19.7) * mm, "end": v(319.42, 15.1) * mm});
            skLineSegment(sketch, "E18.61.0.3", {"start": v(319.42, 15.1) * mm, "end": v(321.96, 15.1) * mm});
            skLineSegment(sketch, "E18.62.0.0", {"start": v(321.96, 19.7) * mm, "end": v(324.5, 19.7) * mm});
            skLineSegment(sketch, "E18.62.0.1", {"start": v(327.04, 15.1) * mm, "end": v(327.04, 19.71) * mm});
            skLineSegment(sketch, "E18.62.0.2", {"start": v(324.5, 19.7) * mm, "end": v(324.5, 15.1) * mm});
            skLineSegment(sketch, "E18.62.0.3", {"start": v(324.5, 15.1) * mm, "end": v(327.04, 15.1) * mm});
            skLineSegment(sketch, "E18.63.0.0", {"start": v(327.04, 19.7) * mm, "end": v(329.58, 19.7) * mm});
            skLineSegment(sketch, "E18.63.0.1", {"start": v(332.12, 15.1) * mm, "end": v(332.12, 19.71) * mm});
            skLineSegment(sketch, "E18.63.0.2", {"start": v(329.58, 19.7) * mm, "end": v(329.58, 15.1) * mm});
            skLineSegment(sketch, "E18.63.0.3", {"start": v(329.58, 15.1) * mm, "end": v(332.12, 15.1) * mm});
            skLineSegment(sketch, "E18.64.0.0", {"start": v(332.12, 19.7) * mm, "end": v(334.66, 19.7) * mm});
            skLineSegment(sketch, "E18.64.0.1", {"start": v(337.2, 15.1) * mm, "end": v(337.2, 19.71) * mm});
            skLineSegment(sketch, "E18.64.0.2", {"start": v(334.66, 19.7) * mm, "end": v(334.66, 15.1) * mm});
            skLineSegment(sketch, "E18.64.0.3", {"start": v(334.66, 15.1) * mm, "end": v(337.2, 15.1) * mm});
            skLineSegment(sketch, "E18.65.0.0", {"start": v(337.2, 19.7) * mm, "end": v(339.74, 19.7) * mm});
            skLineSegment(sketch, "E18.65.0.1", {"start": v(342.28, 15.1) * mm, "end": v(342.28, 19.71) * mm});
            skLineSegment(sketch, "E18.65.0.2", {"start": v(339.74, 19.7) * mm, "end": v(339.74, 15.1) * mm});
            skLineSegment(sketch, "E18.65.0.3", {"start": v(339.74, 15.1) * mm, "end": v(342.28, 15.1) * mm});
            skLineSegment(sketch, "E18.66.0.0", {"start": v(342.28, 19.7) * mm, "end": v(344.82, 19.7) * mm});
            skLineSegment(sketch, "E18.66.0.1", {"start": v(347.36, 15.1) * mm, "end": v(347.36, 19.71) * mm});
            skLineSegment(sketch, "E18.66.0.2", {"start": v(344.82, 19.7) * mm, "end": v(344.82, 15.1) * mm});
            skLineSegment(sketch, "E18.66.0.3", {"start": v(344.82, 15.1) * mm, "end": v(347.36, 15.1) * mm});
            skLineSegment(sketch, "E18.67.0.0", {"start": v(347.36, 19.7) * mm, "end": v(349.9, 19.7) * mm});
            skLineSegment(sketch, "E18.67.0.1", {"start": v(352.44, 15.1) * mm, "end": v(352.44, 19.71) * mm});
            skLineSegment(sketch, "E18.67.0.2", {"start": v(349.9, 19.7) * mm, "end": v(349.9, 15.1) * mm});
            skLineSegment(sketch, "E18.67.0.3", {"start": v(349.9, 15.1) * mm, "end": v(352.44, 15.1) * mm});
            skLineSegment(sketch, "E18.68.0.0", {"start": v(352.44, 19.7) * mm, "end": v(354.98, 19.7) * mm});
            skLineSegment(sketch, "E18.68.0.1", {"start": v(357.52, 15.1) * mm, "end": v(357.52, 19.71) * mm});
            skLineSegment(sketch, "E18.68.0.2", {"start": v(354.98, 19.7) * mm, "end": v(354.98, 15.1) * mm});
            skLineSegment(sketch, "E18.68.0.3", {"start": v(354.98, 15.1) * mm, "end": v(357.52, 15.1) * mm});
            skLineSegment(sketch, "E18.69.0.0", {"start": v(357.52, 19.7) * mm, "end": v(360.06, 19.7) * mm});
            skLineSegment(sketch, "E18.69.0.1", {"start": v(362.6, 15.1) * mm, "end": v(362.6, 19.71) * mm});
            skLineSegment(sketch, "E18.69.0.2", {"start": v(360.06, 19.7) * mm, "end": v(360.06, 15.1) * mm});
            skLineSegment(sketch, "E18.69.0.3", {"start": v(360.06, 15.1) * mm, "end": v(362.6, 15.1) * mm});
            skLineSegment(sketch, "E18.70.0.0", {"start": v(362.6, 19.7) * mm, "end": v(365.14, 19.7) * mm});
            skLineSegment(sketch, "E18.70.0.1", {"start": v(367.68, 15.1) * mm, "end": v(367.68, 19.71) * mm});
            skLineSegment(sketch, "E18.70.0.2", {"start": v(365.14, 19.7) * mm, "end": v(365.14, 15.1) * mm});
            skLineSegment(sketch, "E18.70.0.3", {"start": v(365.14, 15.1) * mm, "end": v(367.68, 15.1) * mm});
            skLineSegment(sketch, "E18.71.0.0", {"start": v(367.68, 19.7) * mm, "end": v(370.22, 19.7) * mm});
            skLineSegment(sketch, "E18.71.0.1", {"start": v(372.76, 15.1) * mm, "end": v(372.76, 19.71) * mm});
            skLineSegment(sketch, "E18.71.0.2", {"start": v(370.22, 19.7) * mm, "end": v(370.22, 15.1) * mm});
            skLineSegment(sketch, "E18.71.0.3", {"start": v(370.22, 15.1) * mm, "end": v(372.76, 15.1) * mm});
            skLineSegment(sketch, "E18.72.0.0", {"start": v(372.76, 19.7) * mm, "end": v(375.3, 19.7) * mm});
            skLineSegment(sketch, "E18.72.0.1", {"start": v(377.84, 15.1) * mm, "end": v(377.84, 19.71) * mm});
            skLineSegment(sketch, "E18.72.0.2", {"start": v(375.3, 19.7) * mm, "end": v(375.3, 15.1) * mm});
            skLineSegment(sketch, "E18.72.0.3", {"start": v(375.3, 15.1) * mm, "end": v(377.84, 15.1) * mm});
            skLineSegment(sketch, "E18.73.0.0", {"start": v(377.84, 19.7) * mm, "end": v(380.38, 19.7) * mm});
            skLineSegment(sketch, "E18.73.0.1", {"start": v(382.92, 15.1) * mm, "end": v(382.92, 19.71) * mm});
            skLineSegment(sketch, "E18.73.0.2", {"start": v(380.38, 19.7) * mm, "end": v(380.38, 15.1) * mm});
            skLineSegment(sketch, "E18.73.0.3", {"start": v(380.38, 15.1) * mm, "end": v(382.92, 15.1) * mm});
            skLineSegment(sketch, "E18.direction1", {"start": v(7, 19.7) * mm, "end": v(12.08, 19.7) * mm, "construction": true});
            skLineSegment(sketch, "E19", {"start": v(-12.84, 0) * mm, "end": v(28.11, 0) * mm, "construction": true});
            skLineSegment(sketch, "E20", {"start": v(382.92, 19.71) * mm, "end": v(384.8, 19.71) * mm});
            skSolve(sketch);
        }
        {
            var Q0;
            Q0=makeQuery(id+"F0.imprint","IMPRINT",FACE,{"disambiguationData":[TD([[makeQuery(id+"F0.imprint","IMPRINT",EDGE,{"derivedFrom":sQuery(id+"F0.wireOp",EDGE,"E0")}),-1.0]])]});
            var Q1;
            Q1=sQuery(id+"F0.wireOp",EDGE,"E19");
            revolve(context, id + "F1", {"entities" : qUnion([Q0]), "axis" : qUnion([Q1]), "revolveType" : RevolveType.FULL});
        }
    });
